FCSTD DOCUMENT  (FreeCAD 0.18R16268 (Git))
Label: asm_Hypnotic
License: All rights reserved
LicenseURL: http://en.wikipedia.org/wiki/All_rights_reserved
objects: PartDesign::CoordinateSystem×4, App::Link×3, App::FeaturePython×3, Sketcher::SketchObject×2, App::DocumentObjectGroup×1, App::Part×1
note: 6 computed .brp shape members not serialized (recipe doc carries the construction recipe); baked Part::Feature solids carry a one-line shape summary decoded from their .brp
EXTERNAL_REF file=Support.fcstd obj=Model
EXTERNAL_REF file=Wheel.fcstd obj=Model
EXTERNAL_REF file=Triangle.fcstd obj=Model

FEATURE [PartDesign::CoordinateSystem] LCS_0
  AttacherType = Attacher::AttachEngine3D
FEATURE [PartDesign::CoordinateSystem] LCS_rot
  AttacherType = Attacher::AttachEngine3D
  AttachmentOffset = pos=(0,0,0) rot=(0,0,1;12.5664rad)
  MapMode = 2
  Support = -> [LCS_0]
FEATURE [Sketcher::SketchObject] Sketch_rot
  MapMode = 2
  Support = -> [LCS_rot]
  sketch-geometry (1):
    g0: LineSegment StartX=0 StartY=0 StartZ=0 EndX=100 EndY=0 EndZ=0
  constraints (3):
    c: Coincident(g0,g-1)
    c: Horizontal(g0)
    c: DistanceX(g0,g0) = 100
FEATURE [Sketcher::SketchObject] Sketch
  ExternalGeometry = -> [Sketch_rot]
  sketch-geometry (16):
    g0: LineSegment StartX=100 StartY=173.205 StartZ=0 EndX=-100 EndY=173.205 EndZ=0
    g1: LineSegment StartX=-100 StartY=173.205 StartZ=0 EndX=-200 EndY=-2.84e-14 EndZ=0
    g2: LineSegment StartX=-200 StartY=-3.76e-14 StartZ=0 EndX=-100 EndY=-173.205 EndZ=0
    g3: LineSegment StartX=-100 StartY=-173.205 StartZ=0 EndX=100 EndY=-173.205 EndZ=0
    g4: LineSegment StartX=100 StartY=-173.205 StartZ=0 EndX=200 EndY=0 EndZ=0
    g5: LineSegment StartX=200 StartY=0 StartZ=0 EndX=100 EndY=173.205 EndZ=0
    g6: Circle [constr] CenterX=0 CenterY=0 CenterZ=0 NormalX=0 NormalY=0 NormalZ=1 AngleXU=0 Radius=200
    g7: LineSegment StartX=-9.43e-14 StartY=-3.3e-15 StartZ=0 EndX=-86.6025 EndY=-150 EndZ=0
    g8: LineSegment StartX=-86.6025 StartY=-150 StartZ=0 EndX=86.6025 EndY=-150 EndZ=0
    g9: LineSegment StartX=86.6025 StartY=-150 StartZ=0 EndX=-9.95e-14 EndY=0 EndZ=0
    g10: Circle [constr] CenterX=0 CenterY=-100 CenterZ=0 NormalX=0 NormalY=0 NormalZ=1 AngleXU=0 Radius=100
    g11: LineSegment [constr] StartX=100 StartY=-173.205 StartZ=0 EndX=-100 EndY=173.205 EndZ=0
    g12: LineSegment [constr] StartX=-200 StartY=-3.76e-14 StartZ=0 EndX=200 EndY=0 EndZ=0
    g13: LineSegment [constr] StartX=-100 StartY=-173.205 StartZ=0 EndX=100 EndY=173.205 EndZ=0
    g14: LineSegment StartX=0 StartY=-100 StartZ=0 EndX=-9.43e-14 EndY=0 EndZ=0
    g15: LineSegment StartX=0 StartY=0 StartZ=0 EndX=200 EndY=0 EndZ=0
  constraints (38):
    c: Coincident(g0,g1)
    c: Coincident(g1,g2)
    c: Coincident(g2,g3)
    c: Coincident(g3,g4)
    c: Coincident(g4,g5)
    c: Coincident(g5,g0)
    c: Equal(g0, g1-g5) x5
    c: PointOnObject(g0,g6)
    c: PointOnObject(g1,g6)
    c: PointOnObject(g2,g6)
    c: PointOnObject(g3,g6)
    c: PointOnObject(g4,g6)
    c: PointOnObject(g5,g6)
    c: Coincident(g7,g8)
    c: Coincident(g8,g9)
    c: Coincident(g9,g7)
    c: Equal(g7,g8)
    c: Equal(g7,g9)
    c: PointOnObject(g7,g10)
    c: PointOnObject(g8,g10)
    c: PointOnObject(g9,g10)
    c: Coincident(g13,g2)
    c: Coincident(g13,g0)
    c: Coincident(g11,g0)
    c: Coincident(g11,g3)
    c: Coincident(g12,g4)
    c: Coincident(g12,g1)
    c: Radius(g6) = 200
    c: Coincident(g6,g-1)
    c: PointOnObject(g7,g13)
    c: PointOnObject(g8,g11)
    c: DistanceX(g10) = 0
    c: DistanceY(g10) = -100
    c: Coincident(g14,g7)
    c: Coincident(g15,g4)
    c: Coincident(g14,g10)
    c: Parallel(g-3,g15)
    c: Coincident(g15,g-1)
FEATURE [PartDesign::CoordinateSystem] LCS_wheel
  AttacherType = Attacher::AttachEngine3D
  AttachmentOffset = pos=(0,0,25) rot=(0,0,1;0rad)
  MapMode = 49
  Placement = pos=(-4.97e-14,-1.6e-15,25) rot=(0,0,1;0rad)
  Support = -> [Sketch]
FEATURE [PartDesign::CoordinateSystem] LCS_triangle
  AttacherType = Attacher::AttachEngine3D
  AttachmentOffset = pos=(0,0,50) rot=(0,0,1;0rad)
  MapMode = 50
  Placement = pos=(0,-100,50) rot=(0,0,1;1.5708rad)
  Support = -> [Sketch]
FEATURE [App::Link] Support
  LinkPlacement = pos=(0,0,0) rot=(-0.57735,-0.57735,-0.57735;2.0944rad)
  LinkedObject = -> <external Support.fcstd>#Model
  Placement = pos=(0,0,0) rot=(-0.57735,-0.57735,-0.57735;2.0944rad)
  expr: Placement = <<LCS_0>>.Placement.multiply(<<constr_Support>>.AttachmentOffset).multiply(.<<LCS_0.>>.Placement.inverse())
FEATURE [App::FeaturePython] constr_Support  # WARN: FeaturePython — macro-defined, semantics opaque (R4)
  AttachedTo = Parent Assembly
  AttachmentLCS = LCS_0
  AttachmentOffset = pos=(0,0,0) rot=(-0.57735,-0.57735,-0.57735;2.0944rad)
  ConstraintType = AttachmentByLCS
  LinkName = Support
  LinkedFile = Support
  LinkedPartLCS = LCS_0
FEATURE [App::Link] Wheel
  LinkPlacement = pos=(-4.97e-14,-1.6e-15,25) rot=(0.250563,-0.935113,0.250563;1.63783rad)
  LinkedObject = -> <external Wheel.fcstd>#Model
  Placement = pos=(-4.97e-14,-1.6e-15,25) rot=(0.250563,-0.935113,0.250563;1.63783rad)
  expr: Placement = <<LCS_wheel>>.Placement.multiply(<<constr_Wheel>>.AttachmentOffset).multiply(.<<LCS_0.>>.Placement.inverse())
FEATURE [App::FeaturePython] constr_Wheel  # WARN: FeaturePython — macro-defined, semantics opaque (R4)
  AttachedTo = Parent Assembly
  AttachmentLCS = LCS_wheel
  AttachmentOffset = pos=(0,0,0) rot=(0.250563,-0.935113,0.250563;1.63783rad)
  ConstraintType = AttachmentByLCS
  LinkName = Wheel
  LinkedFile = Wheel
  LinkedPartLCS = LCS_0
FEATURE [App::Link] Triangle
  LinkPlacement = pos=(0,-100,50) rot=(0.57735,0.57735,0.57735;4.18879rad)
  LinkedObject = -> <external Triangle.fcstd>#Model
  Placement = pos=(0,-100,50) rot=(0.57735,0.57735,0.57735;4.18879rad)
  expr: Placement = <<LCS_triangle>>.Placement.multiply(<<constr_Triangle>>.AttachmentOffset).multiply(.<<LCS_0.>>.Placement.inverse())
FEATURE [App::FeaturePython] constr_Triangle  # WARN: FeaturePython — macro-defined, semantics opaque (R4)
  AttachedTo = Parent Assembly
  AttachmentLCS = LCS_triangle
  AttachmentOffset = pos=(0,0,0) rot=(0.707107,0,0.707107;3.14159rad)
  ConstraintType = AttachmentByLCS
  LinkName = Triangle
  LinkedFile = Triangle
  LinkedPartLCS = LCS_0
FEATURE [App::DocumentObjectGroup] Constraints
  Group = -> [constr_Support,constr_Wheel,constr_Triangle]
FEATURE [App::Part] Model
  Group = -> [Constraints,LCS_0,LCS_rot,Sketch_rot,Sketch,LCS_wheel,LCS_triangle,Support,constr_Support,Wheel,constr_Wheel,Triangle,constr_Triangle]
  Origin = -> Origin

RESOLVED EXTERNAL PARTS (link-assembly join: the EXTERNAL_REF files above that resolve inside this repo's crawl, each included once):
---- part Support.fcstd = doc fcstd_e93ae97ccbc4 ----
FCSTD DOCUMENT  (FreeCAD 0.18R16268 (Git))
Label: Support
License: All rights reserved
LicenseURL: http://en.wikipedia.org/wiki/All_rights_reserved
objects: Sketcher::SketchObject×3, PartDesign::Pad×3, PartDesign::CoordinateSystem×2, App::DocumentObjectGroup×1, PartDesign::Body×1, App::Part×1
note: 12 computed .brp shape members not serialized (recipe doc carries the construction recipe); baked Part::Feature solids carry a one-line shape summary decoded from their .brp

FEATURE [App::DocumentObjectGroup] Constraints
FEATURE [PartDesign::CoordinateSystem] LCS_0
  AttacherType = Attacher::AttachEngine3D
FEATURE [Sketcher::SketchObject] Sketch_0
  MapMode = 4
  Placement = pos=(0,0,0) rot=(0.57735,0.57735,0.57735;2.0944rad)
  Support = -> [LCS_0]
  sketch-geometry (5):
    g0: Circle CenterX=0 CenterY=0 CenterZ=0 NormalX=0 NormalY=0 NormalZ=1 AngleXU=0 Radius=7.5
    g1: ArcOfCircle CenterX=0 CenterY=0 CenterZ=0 NormalX=0 NormalY=0 NormalZ=1 AngleXU=0 Radius=25 StartAngle=0.287525 EndAngle=2.85407
    g2: LineSegment StartX=-23.9737 StartY=7.08949 StartZ=0 EndX=-100 EndY=-250 EndZ=0
    g3: LineSegment StartX=23.9737 StartY=7.08949 StartZ=0 EndX=100 EndY=-250 EndZ=0
    g4: LineSegment StartX=-100 StartY=-250 StartZ=0 EndX=100 EndY=-250 EndZ=0
  constraints (12):
    c: Coincident(g0,g-1)
    c: Coincident(g1,g0)
    c: Symmetric(g1,g1,g-2)
    c: Coincident(g4,g2)
    c: Coincident(g4,g3)
    c: Symmetric(g2,g3,g-2)
    c: Tangent(g2,g1) = -1.5708
    c: Coincident(g1,g3)
    c: Distance(g0,g4) = 250
    c: DistanceX(g4,g4) = 200
    c: Diameter(g0) = 15
    c: Diameter(g1) = 50
FEATURE [PartDesign::CoordinateSystem] LCS_triangle
  AttacherType = Attacher::AttachEngine3D
  AttachmentOffset = pos=(85,0,-100) rot=(0,0,1;0rad)
  MapMode = 2
  Placement = pos=(85,0,-100) rot=(0,0,1;0rad)
  Support = -> [LCS_0]
FEATURE [Sketcher::SketchObject] Sketch_1
  ExternalGeometry = -> [Sketch_0]
  MapMode = 4
  Placement = pos=(85,0,-100) rot=(0.57735,0.57735,0.57735;2.0944rad)
  Support = -> [LCS_triangle]
  sketch-geometry (5):
    g0: Circle CenterX=0 CenterY=0 CenterZ=0 NormalX=0 NormalY=0 NormalZ=1 AngleXU=0 Radius=7.5
    g1: ArcOfCircle CenterX=0 CenterY=0 CenterZ=0 NormalX=0 NormalY=0 NormalZ=1 AngleXU=0 Radius=25 StartAngle=5.63968 EndAngle=10.0683
    g2: LineSegment StartX=-100 StartY=-150 StartZ=0 EndX=-20 EndY=-15 EndZ=0
    g3: LineSegment StartX=20 StartY=-15 StartZ=0 EndX=100 EndY=-150 EndZ=0
    g4: LineSegment StartX=100 StartY=-150 StartZ=0 EndX=-100 EndY=-150 EndZ=0
  constraints (12):
    c: Coincident(g0,g-1)
    c: Coincident(g1,g0)
    c: Symmetric(g1,g1,g-2)
    c: Coincident(g2,g-3)
    c: Coincident(g2,g1)
    c: Coincident(g3,g1)
    c: Coincident(g3,g-3)
    c: Coincident(g4,g3)
    c: Coincident(g4,g2)
    c: Diameter(g0) = 15
    c: Diameter(g1) = 50
    c: DistanceX(g1,g1) = 40
FEATURE [Sketcher::SketchObject] Sketch_2
  ExternalGeometry = -> [Sketch_0]
  MapMode = 4
  Placement = pos=(0,0,0) rot=(0.57735,0.57735,0.57735;2.0944rad)
  Support = -> [LCS_0]
  sketch-geometry (4):
    g0: LineSegment StartX=-100 StartY=-250 StartZ=0 EndX=100 EndY=-250 EndZ=0
    g1: LineSegment StartX=100 StartY=-250 StartZ=0 EndX=100 EndY=-270 EndZ=0
    g2: LineSegment StartX=100 StartY=-270 StartZ=0 EndX=-100 EndY=-270 EndZ=0
    g3: LineSegment StartX=-100 StartY=-270 StartZ=0 EndX=-100 EndY=-250 EndZ=0
  constraints (10):
    c: Coincident(g0,g1)
    c: Coincident(g1,g2)
    c: Coincident(g2,g3)
    c: Coincident(g3,g0)
    c: Horizontal(g2)
    c: Vertical(g1)
    c: Vertical(g3)
    c: Coincident(g0,g-3)
    c: Coincident(g-3,g0)
    c: DistanceY(g1,g1) = 20
FEATURE [PartDesign::Pad] Pad
  ClaimChildren = false
  Length = 10
  Length2 = 100
  Profile = -> Sketch_0
  Type = 0
FEATURE [PartDesign::Pad] Pad001
  BaseFeature = -> Pad
  ClaimChildren = false
  Length = 85
  Length2 = 100
  Profile = -> Sketch_2
  Type = 0
FEATURE [PartDesign::Pad] Pad002
  BaseFeature = -> Pad001
  ClaimChildren = false
  Length = 10
  Length2 = 100
  Profile = -> Sketch_1
  Reversed = true
  Type = 0
FEATURE [PartDesign::Body] Body
  Group = -> [Pad,Pad001,Pad002]
  Origin = -> Origin001
  Tip = -> Pad002
FEATURE [App::Part] Model
  Group = -> [Constraints,LCS_0,Sketch_0,LCS_triangle,Sketch_1,Sketch_2,Body]
  Origin = -> Origin
---- part Triangle.fcstd = doc fcstd_1519f49ed87a ----
FCSTD DOCUMENT  (FreeCAD 0.18R16268 (Git))
Label: Triangle
License: All rights reserved
LicenseURL: http://en.wikipedia.org/wiki/All_rights_reserved
objects: Sketcher::SketchObject×2, PartDesign::Pad×2, App::DocumentObjectGroup×1, PartDesign::CoordinateSystem×1, PartDesign::PolarPattern×1, PartDesign::Body×1, App::Part×1
note: 9 computed .brp shape members not serialized (recipe doc carries the construction recipe); baked Part::Feature solids carry a one-line shape summary decoded from their .brp

FEATURE [App::DocumentObjectGroup] Constraints
FEATURE [PartDesign::CoordinateSystem] LCS_0
  AttacherType = Attacher::AttachEngine3D
FEATURE [Sketcher::SketchObject] Sketch_0
  MapMode = 4
  Placement = pos=(0,0,0) rot=(0.57735,0.57735,0.57735;2.0944rad)
  Support = -> [LCS_0]
  sketch-geometry (5):
    g0: ArcOfCircle CenterX=0 CenterY=0 CenterZ=0 NormalX=0 NormalY=0 NormalZ=1 AngleXU=0 Radius=25 StartAngle=2.0944 EndAngle=7.33038
    g1: ArcOfCircle CenterX=0 CenterY=100 CenterZ=0 NormalX=0 NormalY=0 NormalZ=1 AngleXU=0 Radius=15 StartAngle=5.6975 EndAngle=10.0105
    g2: LineSegment StartX=-12.5 StartY=91.7084 StartZ=0 EndX=-12.5 EndY=21.6506 EndZ=0
    g3: LineSegment StartX=12.5 StartY=91.7084 StartZ=0 EndX=12.5 EndY=21.6506 EndZ=0
    g4: Circle CenterX=0 CenterY=0 CenterZ=0 NormalX=0 NormalY=0 NormalZ=1 AngleXU=0 Radius=7.5
  constraints (16):
    c: Coincident(g0,g-1)
    c: PointOnObject(g1,g-2)
    c: Vertical(g2)
    c: Vertical(g3)
    c: DistanceY(g0,g1) = 100
    c: Diameter(g1) = 30
    c: Diameter(g0) = 50
    c: Coincident(g0,g2)
    c: Coincident(g0,g3)
    c: Coincident(g1,g3)
    c: Coincident(g1,g2)
    c: Coincident(g2,g1)
    c: Symmetric(g0,g0,g-2)
    c: DistanceX(g0,g0) = 25
    c: Coincident(g4,g0)
    c: Diameter(g4) = 15
FEATURE [PartDesign::Pad] Pad
  ClaimChildren = false
  Length = 20
  Length2 = 100
  Profile = -> Sketch_0
  Type = 0
FEATURE [PartDesign::PolarPattern] PolarPattern
  Angle = 360
  Axis = -> Sketch_0 [N_Axis]
  BaseFeature = -> Pad
  Occurrences = 3
  Originals = -> [Pad]
FEATURE [Sketcher::SketchObject] Sketch
  ExternalGeometry = -> [PolarPattern]
  MapMode = 4
  Placement = pos=(0,0,0) rot=(0.57735,0.57735,0.57735;2.0944rad)
  Support = -> [LCS_0]
  sketch-geometry (3):
    g0: Circle CenterX=0 CenterY=100 CenterZ=0 NormalX=0 NormalY=0 NormalZ=1 AngleXU=0 Radius=10
    g1: Circle CenterX=86.6025 CenterY=-50 CenterZ=0 NormalX=0 NormalY=0 NormalZ=1 AngleXU=0 Radius=10
    g2: Circle CenterX=-86.6025 CenterY=-50 CenterZ=0 NormalX=0 NormalY=0 NormalZ=1 AngleXU=0 Radius=10
  constraints (6):
    c: Coincident(g0,g-3)
    c: Coincident(g1,g-4)
    c: Coincident(g2,g-5)
    c: Equal(g1,g2)
    c: Equal(g2,g0)
    c: Diameter(g2) = 20
FEATURE [PartDesign::Pad] Pad001
  BaseFeature = -> PolarPattern
  ClaimChildren = false
  Length = 15
  Length2 = 100
  Profile = -> Sketch
  Reversed = true
  Type = 0
FEATURE [PartDesign::Body] Body
  Group = -> [Pad,PolarPattern,Sketch,Pad001]
  Origin = -> Origin001
  Tip = -> Pad001
FEATURE [App::Part] Model
  Group = -> [Constraints,LCS_0,Sketch_0,Body]
  Origin = -> Origin
---- part Wheel.fcstd = doc fcstd_51c63af066eb ----
FCSTD DOCUMENT  (FreeCAD 0.18R16268 (Git))
Label: Wheel
License: All rights reserved
LicenseURL: http://en.wikipedia.org/wiki/All_rights_reserved
objects: Sketcher::SketchObject×2, PartDesign::Pad×2, App::DocumentObjectGroup×1, PartDesign::CoordinateSystem×1, PartDesign::PolarPattern×1, PartDesign::Body×1, App::Part×1
note: 9 computed .brp shape members not serialized (recipe doc carries the construction recipe); baked Part::Feature solids carry a one-line shape summary decoded from their .brp

FEATURE [App::DocumentObjectGroup] Constraints
FEATURE [PartDesign::CoordinateSystem] LCS_0
  AttacherType = Attacher::AttachEngine3D
FEATURE [Sketcher::SketchObject] Sketch_0
  MapMode = 4
  Placement = pos=(0,0,0) rot=(0.57735,0.57735,0.57735;2.0944rad)
  Support = -> [LCS_0]
  sketch-geometry (2):
    g0: Circle CenterX=0 CenterY=0 CenterZ=0 NormalX=0 NormalY=0 NormalZ=1 AngleXU=0 Radius=210
    g1: Circle CenterX=0 CenterY=0 CenterZ=0 NormalX=0 NormalY=0 NormalZ=1 AngleXU=0 Radius=7.5
  constraints (4):
    c: Coincident(g0,g-1)
    c: Coincident(g1,g0)
    c: Diameter(g1) = 15
    c: Diameter(g0) = 420
FEATURE [Sketcher::SketchObject] Sketch_1
  ExternalGeometry = -> [Sketch_0]
  MapMode = 4
  Placement = pos=(0,0,0) rot=(0.57735,0.57735,0.57735;2.0944rad)
  Support = -> [LCS_0]
  sketch-geometry (7):
    g0: LineSegment [constr] StartX=0 StartY=0 StartZ=0 EndX=210 EndY=0 EndZ=0
    g1: LineSegment [constr] StartX=0 StartY=0 StartZ=0 EndX=105 EndY=181.865 EndZ=0
    g2: LineSegment StartX=113.541 StartY=176.659 StartZ=0 EndX=17.3205 EndY=10 EndZ=0
    g3: LineSegment StartX=209.762 StartY=10 StartZ=0 EndX=17.3205 EndY=10 EndZ=0
    g4: LineSegment [constr] StartX=17.3205 StartY=10 StartZ=0 EndX=17.3205 EndY=0 EndZ=0
    g5: LineSegment [constr] StartX=17.3205 StartY=10 StartZ=0 EndX=8.66025 EndY=15 EndZ=0
    g6: ArcOfCircle CenterX=0 CenterY=0 CenterZ=0 NormalX=0 NormalY=0 NormalZ=1 AngleXU=0 Radius=210 StartAngle=0.0476371 EndAngle=0.99956
  constraints (22):
    c: Coincident(g0,g-1)
    c: PointOnObject(g0,g-3)
    c: Horizontal(g0)
    c: Coincident(g1,g-1)
    c: PointOnObject(g1,g-3)
    c: Angle(g0,g1) = 1.0472
    c: PointOnObject(g2,g-3)
    c: PointOnObject(g3,g-3)
    c: Horizontal(g3)
    c: Parallel(g2,g1)
    c: Coincident(g2,g3)
    c: Coincident(g4,g2)
    c: PointOnObject(g4,g0)
    c: Vertical(g4)
    c: Coincident(g5,g2)
    c: PointOnObject(g5,g1)
    c: Perpendicular(g1,g5)
    c: Equal(g5,g4)
    c: DistanceY(g4,g4) = 10
    c: Coincident(g6,g-1)
    c: Coincident(g6,g2)
    c: PointOnObject(g6,g3)
FEATURE [PartDesign::Pad] Pad
  ClaimChildren = false
  Length = 10
  Length2 = 100
  Profile = -> Sketch_0
  Reversed = true
  Type = 0
FEATURE [PartDesign::Pad] Pad001
  BaseFeature = -> Pad
  ClaimChildren = false
  Length = 20
  Length2 = 100
  Profile = -> Sketch_1
  Type = 0
FEATURE [PartDesign::PolarPattern] PolarPattern
  Angle = 360
  Axis = -> Sketch_1 [N_Axis]
  BaseFeature = -> Pad001
  Occurrences = 6
  Originals = -> [Pad001]
FEATURE [PartDesign::Body] Body
  Group = -> [Pad,Pad001,PolarPattern]
  Origin = -> Origin001
  Tip = -> PolarPattern
FEATURE [App::Part] Model
  Group = -> [Constraints,LCS_0,Sketch_0,Sketch_1,Body]
  Origin = -> Origin
